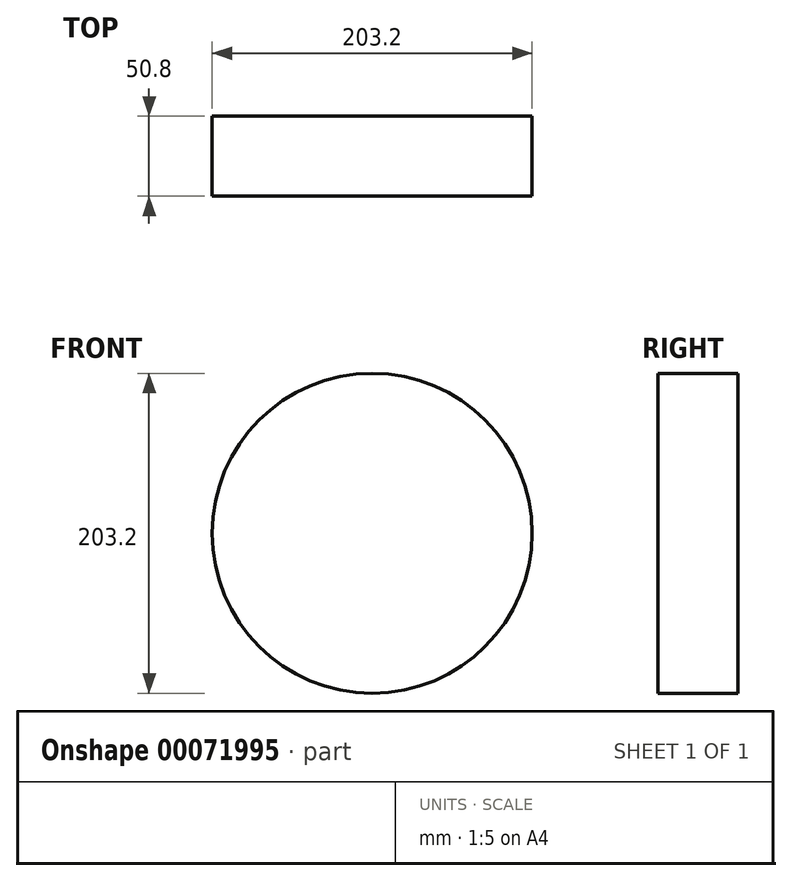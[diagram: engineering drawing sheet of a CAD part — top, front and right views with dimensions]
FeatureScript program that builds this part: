
annotation { "Feature Type Name" : "Feature", "Feature Type Description" : "" }
export const myFeature = defineFeature(function(context is Context, id is Id, definition is map)
    precondition{}
    {
        {
            var Q0;
            Q0=qCreatedBy(makeId("Front.planeOp"),FACE);
            var sketch = newSketch(context, id + "F0", { "sketchPlane" : qUnion([Q0])});
            skCircle(sketch, "E0", {"center": v(0, 0) * mm, "radius": 101.6 * mm});
            skSolve(sketch);
        }
        {
            var Q0;
            Q0=makeQuery(id+"F0.imprint","IMPRINT",FACE,{"disambiguationData":[TD([[makeQuery(id+"F0.imprint","IMPRINT",EDGE,{"derivedFrom":sQuery(id+"F0.wireOp",EDGE,"E0")}),1.0]])]});
            extrude(context, id + "F1", {"entities" : qUnion([Q0]), "depth" : 50.8 * mm});
        }
    });
